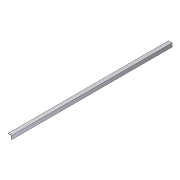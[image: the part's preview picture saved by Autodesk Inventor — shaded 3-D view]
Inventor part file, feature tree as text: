
AUTODESK INVENTOR PART (.ipt)
format: ipt  version: 2012 (Build 160160000, 160)  size: 66,048 bytes
history: native  units: in
note: dims shown in document units (in); Inventor stores cm internally (conversion verified against a paired STEP export)
features: extrude x1, sketch x1
ambient origin geometry x8: Origin, YZ Plane, XZ Plane, XY Plane, X Axis, Y Axis, Z Axis, Center Point
bodies: Solid1 (feature_tree)
feature tree (2):
  extrude  "Extrusion1"  Depth=1.5in
  sketch  "Sketch1"  dims[d0=1.5in d1=1.5in d2=0.125in d3=0.125in d4=65.4375in d5=0.0in]
